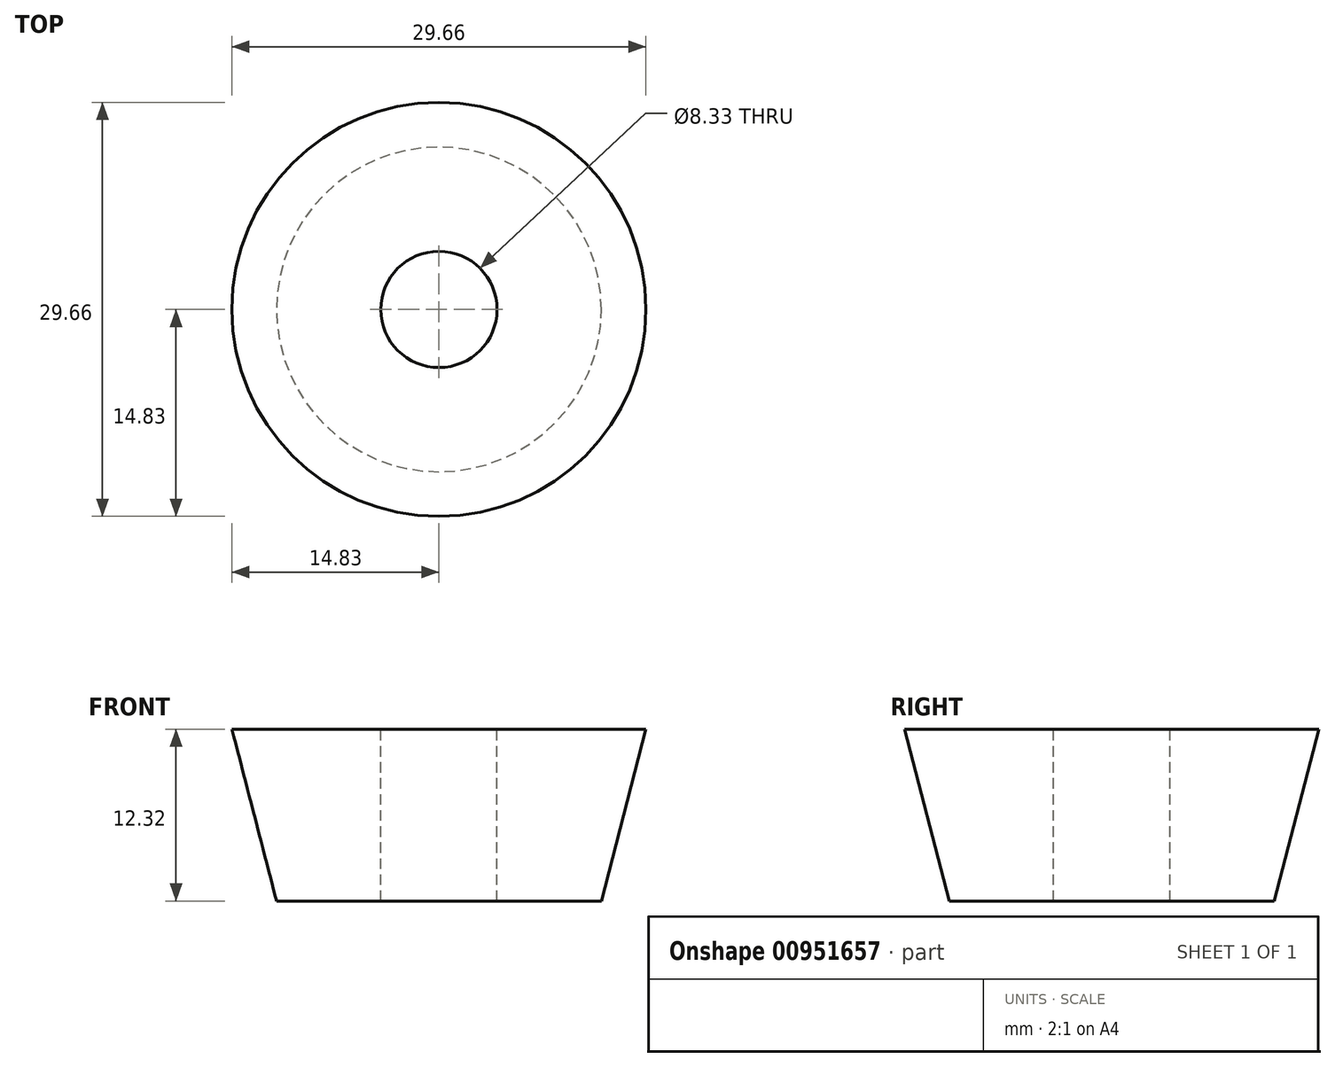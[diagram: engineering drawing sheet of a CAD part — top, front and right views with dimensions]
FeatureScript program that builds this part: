
annotation { "Feature Type Name" : "Feature", "Feature Type Description" : "" }
export const myFeature = defineFeature(function(context is Context, id is Id, definition is map)
    precondition{}
    {
        {
            var Q0;
            Q0=qCreatedBy(makeId("Front.planeOp"),FACE);
            var sketch = newSketch(context, id + "F0", { "sketchPlane" : qUnion([Q0])});
            skLineSegment(sketch, "E0", {"start": v(0, 0) * mm, "end": v(0, -12.32) * mm});
            skSolve(sketch);
        }
        {
            var Q0;
            Q0=qCreatedBy(makeId("Top.planeOp"),FACE);
            var sketch = newSketch(context, id + "F1", { "sketchPlane" : qUnion([Q0])});
            skCircle(sketch, "E1", {"center": v(0, 0) * mm, "radius": 4.17 * mm});
            skSolve(sketch);
        }
        {
            var Q0;
            Q0=qCreatedBy(makeId("Front.planeOp"),FACE);
            var sketch = newSketch(context, id + "F2", { "sketchPlane" : qUnion([Q0])});
            skLineSegment(sketch, "E2", {"start": v(-14.83, 0) * mm, "end": v(-11.63, -12.32) * mm});
            skLineSegment(sketch, "E3", {"start": v(0, 0) * mm, "end": v(-14.83, 0) * mm});
            skLineSegment(sketch, "E4", {"start": v(-11.63, -12.32) * mm, "end": v(0, -12.32) * mm});
            skLineSegment(sketch, "E5", {"start": v(0, -12.32) * mm, "end": v(0, 0) * mm});
            skSolve(sketch);
        }
        {
            var Q0;
            Q0 = qSketchRegion(id + "F2", true);
            var Q1;
            Q1=sQuery(id+"F2.wireOp",EDGE,"E5");
            revolve(context, id + "F3", {"surfaceOperationType" : NewSurfaceOperationType.NEW, "entities" : qUnion([Q0]), "axis" : qUnion([Q1]), "revolveType" : RevolveType.FULL});
        }
        {
            var Q0;
            Q0 = qSketchRegion(id + "F1", true);
            extrude(context, id + "F4", {"entities" : qUnion([Q0]), "operationType" : NewBodyOperationType.REMOVE, "endBound" : BoundingType.UP_TO_NEXT, "oppositeDirection" : true, "depth" : 25.4 * mm, "offsetDistance" : 25.4 * mm});
        }
    });
